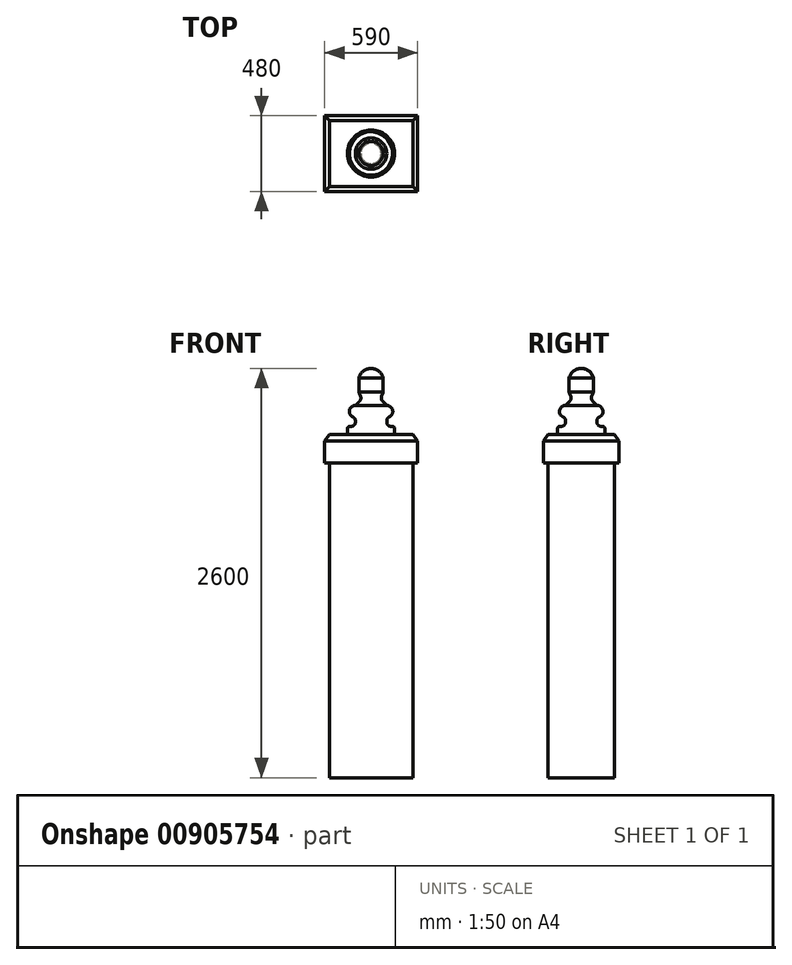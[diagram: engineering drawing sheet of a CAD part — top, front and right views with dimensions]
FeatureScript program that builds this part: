
annotation { "Feature Type Name" : "Feature", "Feature Type Description" : "" }
export const myFeature = defineFeature(function(context is Context, id is Id, definition is map)
    precondition{}
    {
        {
            var Q0;
            Q0=qCreatedBy(makeId("Top.planeOp"),FACE);
            var sketch = newSketch(context, id + "F0", { "sketchPlane" : qUnion([Q0])});
            skLineSegment(sketch, "E0.bottom", {"start": v(-265, 210) * mm, "end": v(265, 210) * mm});
            skLineSegment(sketch, "E0.top", {"start": v(-265, -210) * mm, "end": v(265, -210) * mm});
            skLineSegment(sketch, "E0.left", {"start": v(-265, 210) * mm, "end": v(-265, -210) * mm});
            skLineSegment(sketch, "E0.right", {"start": v(265, 210) * mm, "end": v(265, -210) * mm});
            skSolve(sketch);
        }
        {
            var Q0;
            Q0=qSketchRegion(id+"F0",true);
            extrude(context, id + "F1", {"entities" : qUnion([Q0]), "depth" : 2000 * mm, "offsetDistance" : 25.4 * mm});
        }
        {
            var Q0;
            Q0=makeQuery(id+"F1.opExtrude","CAP_FACE",FACE,{"disambiguationData":[OSD([sQuery(id+"F0.wireOp",EDGE,"E0.bottom"),sQuery(id+"F0.wireOp",EDGE,"E0.top"),sQuery(id+"F0.wireOp",EDGE,"E0.left"),sQuery(id+"F0.wireOp",EDGE,"E0.right")])],"isStart":false});
            var sketch = newSketch(context, id + "F2", { "sketchPlane" : qUnion([Q0])});
            skLineSegment(sketch, "E1.bottom", {"start": v(-295, 240) * mm, "end": v(295, 240) * mm});
            skLineSegment(sketch, "E1.top", {"start": v(-295, -240) * mm, "end": v(295, -240) * mm});
            skLineSegment(sketch, "E1.left", {"start": v(-295, 240) * mm, "end": v(-295, -240) * mm});
            skLineSegment(sketch, "E1.right", {"start": v(295, 240) * mm, "end": v(295, -240) * mm});
            skSolve(sketch);
        }
        {
            var Q0;
            Q0=qSketchRegion(id+"F2",true);
            extrude(context, id + "F3", {"entities" : qUnion([Q0]), "operationType" : NewBodyOperationType.ADD, "depth" : 100 * mm, "offsetDistance" : 25.4 * mm});
        }
        {
            var Q0;
            Q0=qCreatedBy(makeId("Right.planeOp"),FACE);
            var sketch = newSketch(context, id + "F4", { "sketchPlane" : qUnion([Q0])});
            skLineSegment(sketch, "E2.0", {"start": v(-240, 2100) * mm, "end": v(-240, 2000) * mm, "construction": true});
            skLineSegment(sketch, "E3.0", {"start": v(240, 2100) * mm, "end": v(-240, 2100) * mm, "construction": true});
            skLineSegment(sketch, "E4", {"start": v(-240, 2100) * mm, "end": v(-240, 2140) * mm});
            skLineSegment(sketch, "E5", {"start": v(-240, 2100) * mm, "end": v(-210, 2100) * mm});
            skLineSegment(sketch, "E6", {"start": v(-210, 2100) * mm, "end": v(-210, 2180) * mm});
            skLineSegment(sketch, "E7", {"start": v(-304.56, 2140) * mm, "end": v(-240, 2140) * mm, "construction": true});
            skLineSegment(sketch, "E8", {"start": v(-210, 2180) * mm, "end": v(-250, 2180) * mm, "construction": true});
            skLineSegment(sketch, "E9", {"start": v(-250, 2180) * mm, "end": v(-250, 2180) * mm});
            skLineSegment(sketch, "E10", {"start": v(-250, 2180) * mm, "end": v(-290, 2180) * mm, "construction": true});
            skLineSegment(sketch, "E11", {"start": v(-290, 2180) * mm, "end": v(-304.56, 2140) * mm, "construction": true});
            skLineSegment(sketch, "E12", {"start": v(-240, 2140) * mm, "end": v(-210, 2180) * mm});
            skSolve(sketch);
        }
        {
            var Q0;
            Q0=qSketchRegion(id+"F4",true);
            var Q1;
            Q1=makeQuery(id+"F3.opExtrude","CAP_EDGE",EDGE,{"disambiguationData":[OSD([sQuery(id+"F2.wireOp",EDGE,"E1.top")])],"isStart":false});
            var Q2;
            Q2=makeQuery(id+"F3.opExtrude","CAP_EDGE",EDGE,{"disambiguationData":[OSD([sQuery(id+"F2.wireOp",EDGE,"E1.right")])],"isStart":false});
            var Q3;
            Q3=makeQuery(id+"F3.opExtrude","CAP_EDGE",EDGE,{"disambiguationData":[OSD([sQuery(id+"F2.wireOp",EDGE,"E1.bottom")])],"isStart":false});
            var Q4;
            Q4=makeQuery(id+"F3.opExtrude","CAP_EDGE",EDGE,{"disambiguationData":[OSD([sQuery(id+"F2.wireOp",EDGE,"E1.left")])],"isStart":false});
            sweep(context, id + "F5", {"profiles" : qUnion([Q0]), "path" : qUnion([Q1, Q2, Q3, Q4])});
        }
        {
            var Q0;
            Q0=makeQuery(id+"F5.opSweep","SWEPT_FACE",FACE,{"disambiguationData":[OSD([sQuery(id+"F2.wireOp",EDGE,"E1.right"),sQuery(id+"F4.wireOp",EDGE,"E6")])]});
            var sketch = newSketch(context, id + "F6", { "sketchPlane" : qUnion([Q0])});
            skLineSegment(sketch, "E13.0", {"start": v(210, 2180) * mm, "end": v(210, 2100) * mm});
            skLineSegment(sketch, "E13.1", {"start": v(210, 2180) * mm, "end": v(-210, 2180) * mm});
            skLineSegment(sketch, "E13.2", {"start": v(210, 2100) * mm, "end": v(-210, 2100) * mm});
            skLineSegment(sketch, "E13.3", {"start": v(-210, 2180) * mm, "end": v(-210, 2100) * mm});
            skSolve(sketch);
        }
        {
            var Q0;
            Q0=qSketchRegion(id+"F6",true);
            var Q1;
            Q1=makeQuery(id+"F5.opSweep","SWEPT_FACE",FACE,{"disambiguationData":[OSD([sQuery(id+"F2.wireOp",EDGE,"E1.left"),sQuery(id+"F4.wireOp",EDGE,"E6")])]});
            var Q2;
            Q2=makeQuery(id+"F5.opSweep","MID_CAP_VERTEX",VERTEX,{"disambiguationData":[OSD([sQuery(id+"F2.wireOp",EDGE,"E1.bottom"),sQuery(id+"F4.wireOp",EDGE,"E5"),sQuery(id+"F4.wireOp",EDGE,"E6")])],"capPos":2.0});
            extrude(context, id + "F7", {"entities" : qUnion([Q0]), "operationType" : NewBodyOperationType.ADD, "endBound" : BoundingType.UP_TO_SURFACE, "depth" : 25.4 * mm, "endBoundEntityFace" : qUnion([Q1]), "endBoundEntityVertex" : qUnion([Q2]), "offsetDistance" : 25.4 * mm});
        }
        {
            var Q0;
            Q0=qCreatedBy(makeId("Right.planeOp"),FACE);
            var sketch = newSketch(context, id + "F8", { "sketchPlane" : qUnion([Q0])});
            skLineSegment(sketch, "E14", {"start": v(0, 0) * mm, "end": v(0, 2600) * mm, "construction": true});
            skLineSegment(sketch, "E15.0", {"start": v(-50, 2180) * mm, "end": v(50, 2180) * mm, "construction": true});
            skLineSegment(sketch, "E16", {"start": v(0, 2180) * mm, "end": v(150, 2180) * mm});
            skLineSegment(sketch, "E17", {"start": v(100, 2180) * mm, "end": v(100, 2234.4) * mm, "construction": true});
            skLineSegment(sketch, "E18", {"start": v(0, 2600) * mm, "end": v(0, 2180) * mm});
            skArc(sketch, "E19", {"start": v(77.27, 2540.7) * mm, "mid": v(48.7, 2583.47) * mm, "end": v(0, 2600) * mm});
            skLineSegment(sketch, "E20", {"start": v(0, 2520) * mm, "end": v(77.27, 2540.7) * mm, "construction": true});
            skLineSegment(sketch, "E21", {"start": v(0, 2520) * mm, "end": v(80, 2520) * mm, "construction": true});
            skArc(sketch, "E22", {"start": v(0, 2390) * mm, "mid": v(28.97, 2395.43) * mm, "end": v(54.01, 2410.99) * mm, "construction": true});
            skLineSegment(sketch, "E23", {"start": v(0, 2470) * mm, "end": v(77.27, 2449.3) * mm, "construction": true});
            skLineSegment(sketch, "E24", {"start": v(77.27, 2540.7) * mm, "end": v(77.27, 2449.3) * mm});
            skArc(sketch, "E25", {"start": v(100, 2288.8) * mm, "mid": v(138.1, 2326.9) * mm, "end": v(100, 2365) * mm});
            skLineSegment(sketch, "E26", {"start": v(54.01, 2410.99) * mm, "end": v(65, 2400) * mm, "construction": true});
            skArc(sketch, "E27", {"start": v(54.01, 2410.99) * mm, "mid": v(59.83, 2416.9) * mm, "end": v(65, 2423.36) * mm, "construction": true});
            skLineSegment(sketch, "E28", {"start": v(65, 2423.36) * mm, "end": v(65, 2400) * mm});
            skArc(sketch, "E29", {"start": v(65, 2423.36) * mm, "mid": v(72.3, 2435.77) * mm, "end": v(77.27, 2449.3) * mm});
            skLineSegment(sketch, "E30", {"start": v(65, 2400) * mm, "end": v(100, 2365) * mm});
            skLineSegment(sketch, "E31", {"start": v(150, 2180) * mm, "end": v(150, 2230.03) * mm});
            skLineSegment(sketch, "E32", {"start": v(150, 2230.03) * mm, "end": v(100, 2234.4) * mm});
            skLineSegment(sketch, "E33", {"start": v(100, 2234.4) * mm, "end": v(100, 2288.8) * mm});
            skSolve(sketch);
        }
        {
            var Q0;
            Q0=qSketchRegion(id+"F8",true);
            var Q1;
            Q1=sQuery(id+"F8.wireOp",EDGE,"E14");
            revolve(context, id + "F9", {"operationType" : NewBodyOperationType.ADD, "surfaceOperationType" : NewSurfaceOperationType.NEW, "entities" : qUnion([Q0]), "axis" : qUnion([Q1]), "revolveType" : RevolveType.FULL});
        }
        {
            var Q0;
            Q0=makeQuery(id+"F9.opRevolve","SWEPT_EDGE",EDGE,{"disambiguationData":[OSD([sQuery(id+"F8.wireOp",EDGE,"E32"),sQuery(id+"F8.wireOp",EDGE,"E33")])]});
            var Q1;
            Q1=makeQuery(id+"F9.opRevolve","SWEPT_EDGE",EDGE,{"disambiguationData":[OSD([sQuery(id+"F8.wireOp",EDGE,"E25"),sQuery(id+"F8.wireOp",EDGE,"E33")])]});
            var Q2;
            Q2=makeQuery(id+"F9.opRevolve","SWEPT_EDGE",EDGE,{"disambiguationData":[OSD([sQuery(id+"F8.wireOp",EDGE,"E28"),sQuery(id+"F8.wireOp",EDGE,"E29")])]});
            var Q3;
            Q3=makeQuery(id+"F9.opRevolve","SWEPT_EDGE",EDGE,{"disambiguationData":[OSD([sQuery(id+"F8.wireOp",EDGE,"E28"),sQuery(id+"F8.wireOp",EDGE,"E30")])]});
            fillet(context, id + "F10", {"entities" : qUnion([Q0, Q1, Q2, Q3]), "radius" : 25.4 * mm, "tangentPropagation" : true, "allowEdgeOverflow" : false});
        }
        {
            var Q0;
            Q0=makeQuery(id+"F9.opRevolve","SWEPT_EDGE",EDGE,{"disambiguationData":[OSD([sQuery(id+"F8.wireOp",EDGE,"E31"),sQuery(id+"F8.wireOp",EDGE,"E32")])]});
            fillet(context, id + "F11", {"entities" : qUnion([Q0]), "radius" : 12.7 * mm, "tangentPropagation" : true, "allowEdgeOverflow" : false});
        }
    });
